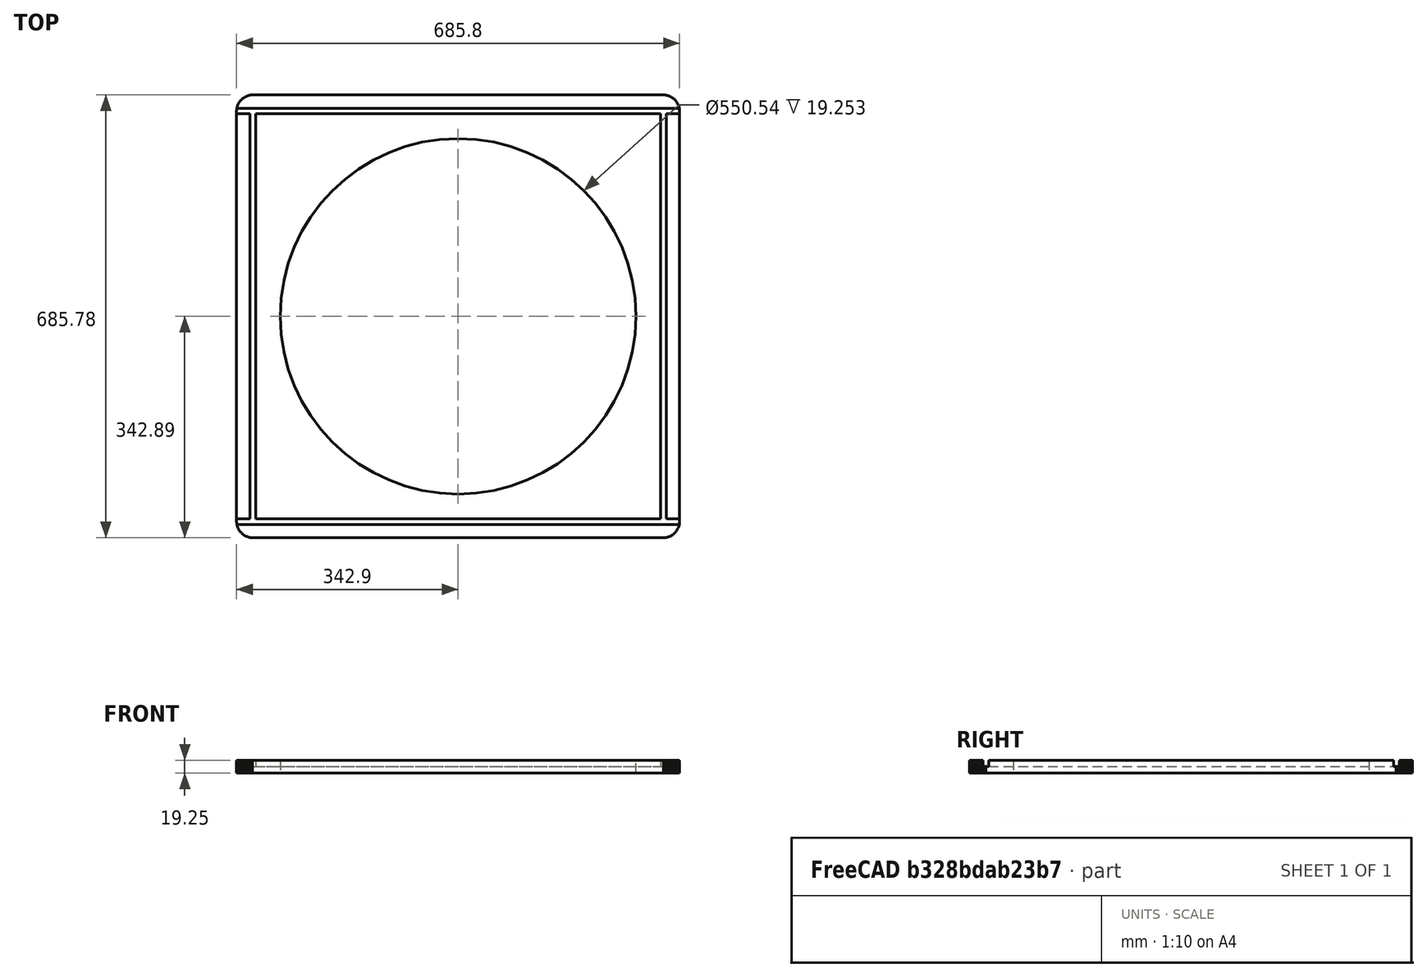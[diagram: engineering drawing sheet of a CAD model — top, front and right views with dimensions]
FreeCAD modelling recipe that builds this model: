
FCSTD DOCUMENT  (FreeCAD 0.21R33771 (Git))
Label: front_panel_try3
License: All rights reserved
LicenseURL: http://en.wikipedia.org/wiki/All_rights_reserved
objects: Part::Box×5, Part::Cylinder×2, Part::FeaturePython×1, Part::MultiFuse×1, Part::Cut×1
note: 10 computed .brp shape members not serialized (recipe doc carries the construction recipe); baked Part::Feature solids carry a one-line shape summary decoded from their .brp

FEATURE [Part::Box] cube
  AttacherType = Attacher::AttachEngine3D
  Height = 9.6266
  Length = 635
  Width = 635
FEATURE [Part::Cylinder] cylinder
  Angle = 360
  AttacherType = Attacher::AttachEngine3D
  FirstAngle = 0
  Height = 9.6266
  Radius = 25.4
  SecondAngle = 0
FEATURE [Part::FeaturePython] minkowski  # WARN: FeaturePython — macro-defined, semantics opaque (R4)
  Arguments = {'convexity': '0'}
  Children = -> [cube,cylinder]
  Operation = minkowski
  Placement = pos=(25.4,25.4,0) rot=(0,0,1;0rad)
FEATURE [Part::Cylinder] cylinder001
  Angle = 360
  AttacherType = Attacher::AttachEngine3D
  FirstAngle = 0
  Height = 254
  Placement = pos=(342.9,342.9,-127) rot=(0,0,1;0rad)
  Radius = 275.272
  SecondAngle = 0
FEATURE [Part::Box] cube001
  AttacherType = Attacher::AttachEngine3D
  Height = 10.525
  Length = 736.6
  Placement = pos=(-25.4,20.6375,9.7282) rot=(0,0,1;0rad)
  Width = 8.73125
FEATURE [Part::Box] cube002
  AttacherType = Attacher::AttachEngine3D
  Height = 10.525
  Length = 736.6
  Placement = pos=(-25.4,656.431,9.7282) rot=(0,0,1;0rad)
  Width = 8.73125
FEATURE [Part::Box] cube003
  AttacherType = Attacher::AttachEngine3D
  Height = 10.525
  Length = 8.73125
  Placement = pos=(20.6375,29.2687,9.7282) rot=(0,0,1;0rad)
  Width = 627.539
FEATURE [Part::Box] cube004
  AttacherType = Attacher::AttachEngine3D
  Height = 10.525
  Length = 8.73125
  Placement = pos=(656.431,29.2687,9.7282) rot=(0,0,1;0rad)
  Width = 627.539
FEATURE [Part::MultiFuse] union
  Shapes = -> [cylinder001,cube001,cube002,cube003,cube004]
FEATURE [Part::Cut] difference
  Base = -> minkowski
  Placement = pos=(0,0,-19.2532) rot=(0,0,1;0rad)
  Tool = -> union
